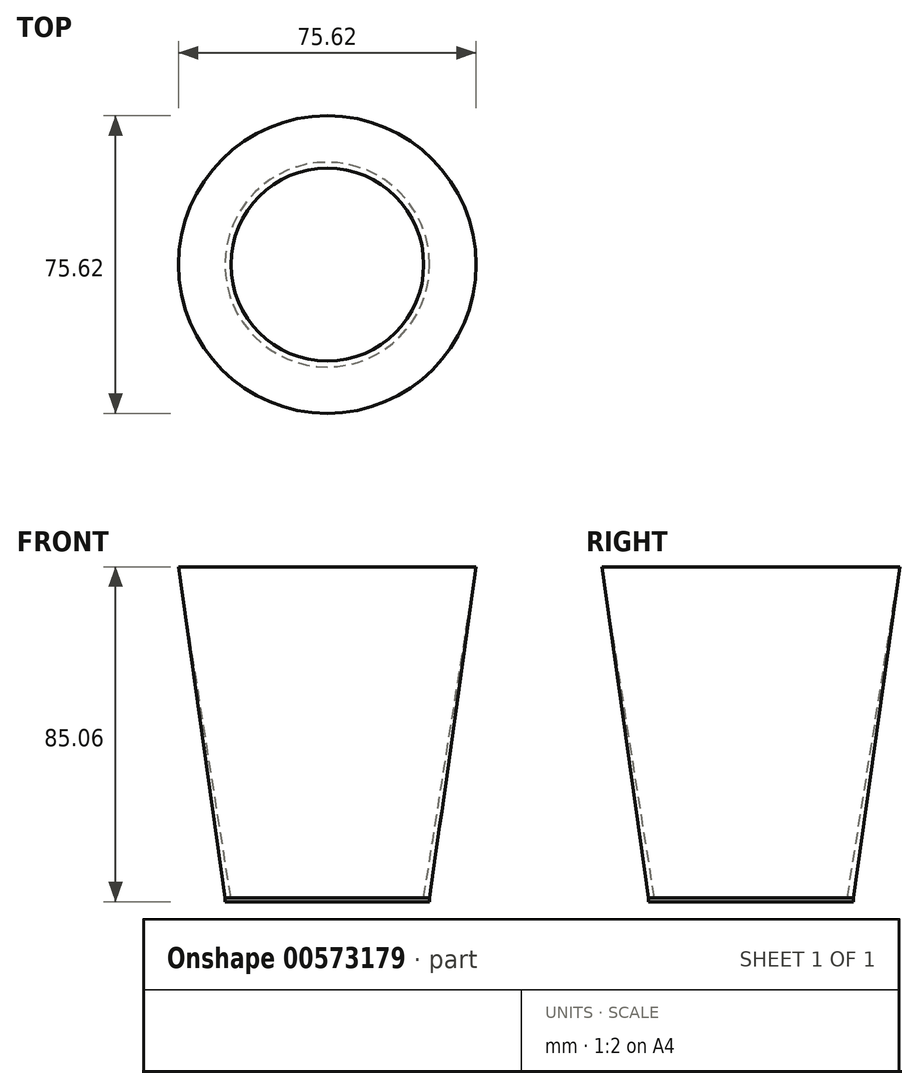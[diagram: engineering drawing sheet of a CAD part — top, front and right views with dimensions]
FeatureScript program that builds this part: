
annotation { "Feature Type Name" : "Feature", "Feature Type Description" : "" }
export const myFeature = defineFeature(function(context is Context, id is Id, definition is map)
    precondition{}
    {
        {
            var Q0;
            Q0=qCreatedBy(makeId("Top.planeOp"),FACE);
            var sketch = newSketch(context, id + "F0", { "sketchPlane" : qUnion([Q0])});
            skCircle(sketch, "E0", {"center": v(0, 0) * mm, "radius": 26 * mm});
            skSolve(sketch);
        }
        {
            var Q0;
            Q0 = qSketchRegion(id + "F0", true);
            var Q1;
            Q1 = qConstructionFilter(qBodyType(qCreatedBy(id + "F0" ,EDGE), BodyType.WIRE), ConstructionObject.NO);
            var Q2;
            Q2 = qConstructionFilter(qBodyType(qCreatedBy(id + "Fzfny7nAQxkXUjQ_0" ,EDGE), BodyType.WIRE), ConstructionObject.NO);
            extrude(context, id + "F1", {"entities" : qUnion([Q0]), "surfaceEntities" : qUnion([Q1, Q2]), "depth" : 115 * mm, "offsetDistance" : 25 * mm, "hasDraft" : true, "draftAngle" : 8 * degree, "hasSecondDirection" : true, "secondDirectionOppositeDirection" : true, "secondDirectionDepth" : 1 * mm});
        }
        {
            var Q0;
            Q0=qCreatedBy(makeId("Top.planeOp"),FACE);
            var sketch = newSketch(context, id + "F2", { "sketchPlane" : qUnion([Q0])});
            skCircle(sketch, "E1", {"center": v(0, 0) * mm, "radius": 24.5 * mm});
            skSolve(sketch);
        }
        {
            var Q0;
            Q0 = qSketchRegion(id + "F2", true);
            extrude(context, id + "F3", {"entities" : qUnion([Q0]), "operationType" : NewBodyOperationType.REMOVE, "depth" : 115 * mm, "offsetDistance" : 25 * mm, "hasDraft" : true, "draftAngle" : 9 * degree});
        }
    });
